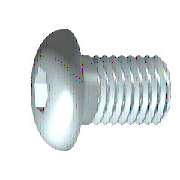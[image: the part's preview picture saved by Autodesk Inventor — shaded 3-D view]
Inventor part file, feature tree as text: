
AUTODESK INVENTOR PART (.ipt)
format: ipt  version: 2014 (Build 180170000, 170)  size: 200,192 bytes
history: native  units: mm (DEFAULTED — no unit token found)
features: sketch x2, extrude x1, plane x1, fillet x1
ambient origin geometry x7: Origin, YZ Plane, XY Plane, X Axis, Y Axis, Z Axis, Center Point
bodies: Solid1 (feature_tree), Body (feature_tree)
feature tree (5):
  extrude  "Slot"  Depth=3.3528mm
  plane  "Work Plane1"
  fillet  "Fillet2"  Radius=3.3528mm
  sketch  "Sketch1"  dims[d1=10.1598mm d2=2.5401mm d3=3.3528mm]
  sketch  "Sketch2"  dims[d4=2.2098mm d5=60.0deg d6=6.35mm d7=6.35mm d8=4.575385mm d9=11.0998mm d10=90.0deg d11=10.0mm d12=0.0mm d13=10.1598mm d14=0.0mm d15=0.779018mm d16=0.779018mm d17=2.9718mm d19=0.0mm d26=12.7mm d27=45.0deg d28=0.0mm d29=0.0mm d30=0.1mm]
